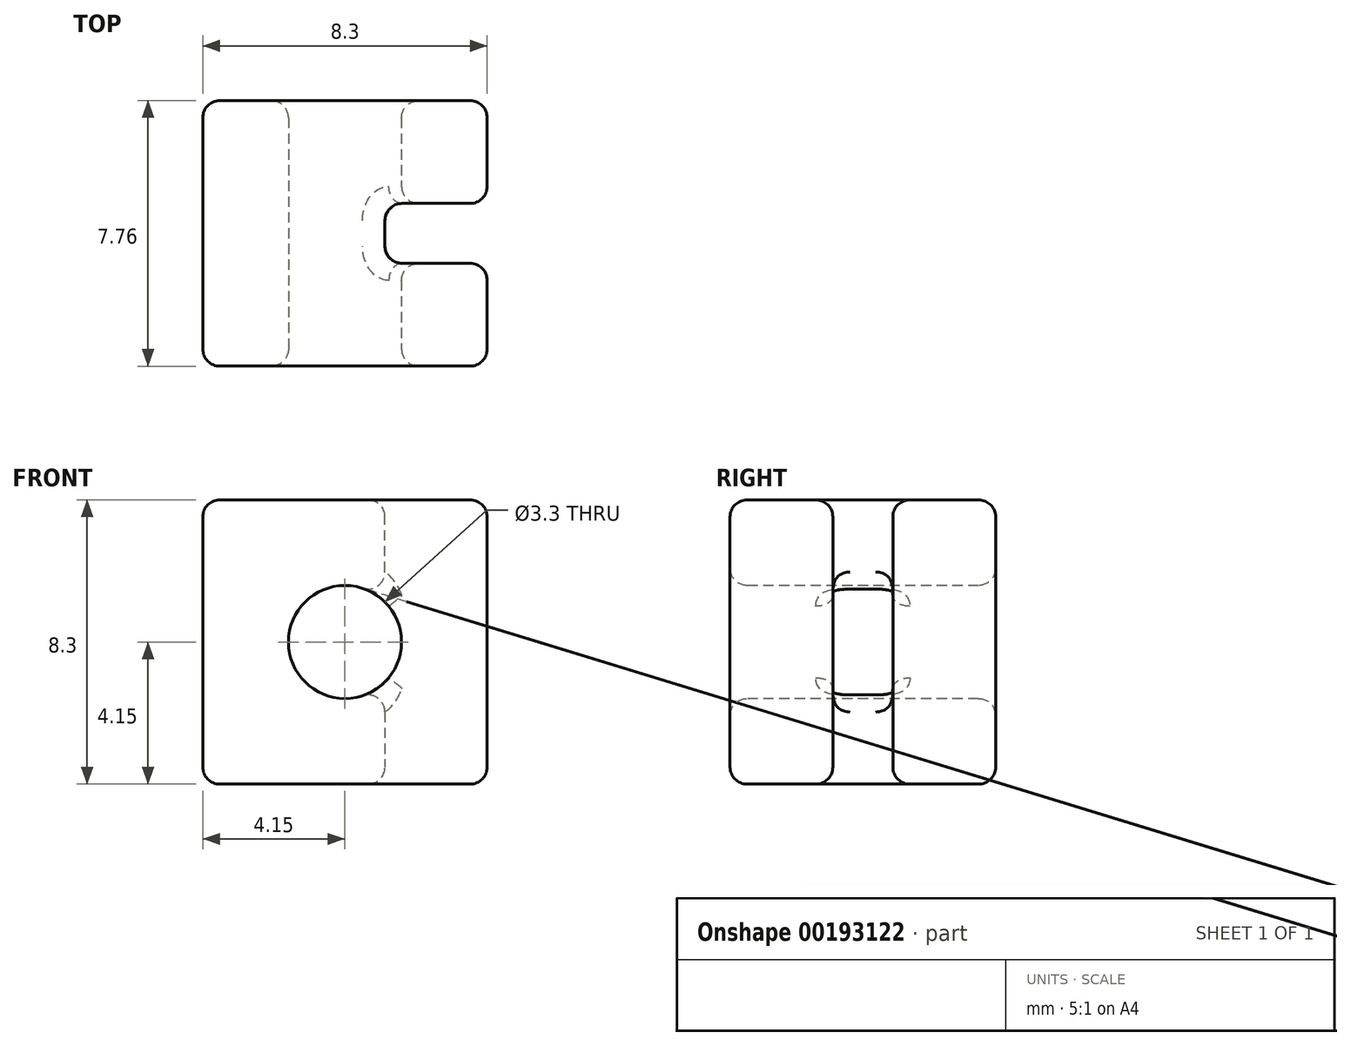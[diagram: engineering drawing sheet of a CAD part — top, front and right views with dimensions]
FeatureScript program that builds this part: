
annotation { "Feature Type Name" : "Feature", "Feature Type Description" : "" }
export const myFeature = defineFeature(function(context is Context, id is Id, definition is map)
    precondition{}
    {
        {
            var Q0;
            Q0=qCreatedBy(makeId("Front.planeOp"),FACE);
            var sketch = newSketch(context, id + "F0", { "sketchPlane" : qUnion([Q0])});
            skCircle(sketch, "E0", {"center": v(0, 0) * mm, "radius": 1.65 * mm});
            skLineSegment(sketch, "E1.bottom", {"start": v(-4.15, 4.15) * mm, "end": v(4.15, 4.15) * mm});
            skLineSegment(sketch, "E1.top", {"start": v(-4.15, -4.15) * mm, "end": v(4.15, -4.15) * mm});
            skLineSegment(sketch, "E1.left", {"start": v(-4.15, 4.15) * mm, "end": v(-4.15, -4.15) * mm});
            skLineSegment(sketch, "E1.right", {"start": v(4.15, 4.15) * mm, "end": v(4.15, -4.15) * mm});
            skLineSegment(sketch, "E2", {"start": v(-4.15, 4.15) * mm, "end": v(4.15, -4.15) * mm, "construction": true});
            skLineSegment(sketch, "E3", {"start": v(-4.15, -4.15) * mm, "end": v(4.15, 4.15) * mm, "construction": true});
            skPoint(sketch, "E4", {"position": v(1.17, 1.17) * mm});
            skPoint(sketch, "E5", {"position": v(1.17, -1.17) * mm});
            skLineSegment(sketch, "E6", {"start": v(1.17, 1.17) * mm, "end": v(1.17, 4.15) * mm});
            skLineSegment(sketch, "E7", {"start": v(1.17, -1.17) * mm, "end": v(1.17, -4.15) * mm});
            skSolve(sketch);
        }
        {
            var Q0;
            Q0=qCreatedBy(makeId("Right.planeOp"),FACE);
            var sketch = newSketch(context, id + "F1", { "sketchPlane" : qUnion([Q0])});
            skLineSegment(sketch, "E8.bottom", {"start": v(-0.87, -4.15) * mm, "end": v(0.87, -4.15) * mm});
            skLineSegment(sketch, "E8.top", {"start": v(-0.87, 4.15) * mm, "end": v(0.87, 4.15) * mm});
            skLineSegment(sketch, "E8.left", {"start": v(-0.87, -4.15) * mm, "end": v(-0.87, 4.15) * mm});
            skLineSegment(sketch, "E8.right", {"start": v(0.88, -4.15) * mm, "end": v(0.88, 4.15) * mm});
            skPoint(sketch, "E8.middle", {"position": v(0, 0) * mm});
            skLineSegment(sketch, "E9.bottom", {"start": v(3.87, 4.15) * mm, "end": v(0.87, 4.15) * mm});
            skLineSegment(sketch, "E9.top", {"start": v(3.88, -4.15) * mm, "end": v(0.87, -4.15) * mm});
            skLineSegment(sketch, "E9.left", {"start": v(3.87, 4.15) * mm, "end": v(3.88, -4.15) * mm});
            skLineSegment(sketch, "E9.right", {"start": v(0.88, 4.15) * mm, "end": v(0.88, -4.15) * mm});
            skLineSegment(sketch, "E10.bottom", {"start": v(-0.88, 4.15) * mm, "end": v(-3.87, 4.15) * mm});
            skLineSegment(sketch, "E10.top", {"start": v(-0.87, -4.15) * mm, "end": v(-3.87, -4.15) * mm});
            skLineSegment(sketch, "E10.left", {"start": v(-0.88, 4.15) * mm, "end": v(-0.87, -4.15) * mm});
            skLineSegment(sketch, "E10.right", {"start": v(-3.87, 4.15) * mm, "end": v(-3.87, -4.15) * mm});
            skSolve(sketch);
        }
        {
            var Q0;
            {var subQ0=sQuery(id+"F0.wireOp",EDGE,"E1.left");Q0=makeQuery(id+"F0.imprint","IMPRINT",FACE,{"disambiguationData":[TD([[makeQuery(id+"F0.imprint","IMPRINT",EDGE,{"derivedFrom":subQ0}),1.0]])]});}
            var Q1;
            Q1=sQuery(id+"F1.wireOp",VERTEX,"E9.bottom.end");
            var Q2;
            Q2=sQuery(id+"F1.wireOp",VERTEX,"E8.left.end");
            extrude(context, id + "F2", {"entities" : qUnion([Q0]), "endBound" : BoundingType.UP_TO_VERTEX, "oppositeDirection" : true, "endBoundEntityVertex" : qUnion([Q1]), "depth" : 25 * mm, "hasSecondDirection" : true, "secondDirectionBound" : SecondDirectionBoundingType.UP_TO_VERTEX, "secondDirectionOppositeDirection" : false, "secondDirectionBoundEntityVertex" : qUnion([Q2]), "secondDirectionDepth" : 25 * mm});
        }
        {
            var Q0;
            Q0 = qSketchRegion(id + "F0", true);
            var Q1;
            Q1=sQuery(id+"F1.wireOp",VERTEX,"E9.left.start");
            var Q2;
            Q2=makeQuery(id+"F2.opExtrude","CAP_FACE",FACE,{"disambiguationData":[OSD([sQuery(id+"F0.wireOp",EDGE,"E0"),sQuery(id+"F0.wireOp",EDGE,"E1.bottom"),sQuery(id+"F0.wireOp",EDGE,"E1.top"),sQuery(id+"F0.wireOp",EDGE,"E1.left"),sQuery(id+"F0.wireOp",EDGE,"E6"),sQuery(id+"F0.wireOp",EDGE,"E7")])],"isStart":false});
            extrude(context, id + "F3", {"entities" : qUnion([Q0]), "operationType" : NewBodyOperationType.ADD, "endBound" : BoundingType.UP_TO_VERTEX, "oppositeDirection" : true, "endBoundEntityVertex" : qUnion([Q1]), "depth" : 3.25 * mm, "hasSecondDirection" : true, "secondDirectionBound" : SecondDirectionBoundingType.UP_TO_SURFACE, "secondDirectionOppositeDirection" : true, "secondDirectionBoundEntityFace" : qUnion([Q2]), "secondDirectionDepth" : 2.3 * mm});
        }
        {
            var Q0;
            Q0 = qSketchRegion(id + "F0", true);
            var Q1;
            Q1=sQuery(id+"F1.wireOp",VERTEX,"E10.bottom.end");
            var Q2;
            Q2=makeQuery(id+"F2.opExtrude","CAP_FACE",FACE,{"disambiguationData":[OSD([sQuery(id+"F0.wireOp",EDGE,"E0"),sQuery(id+"F0.wireOp",EDGE,"E1.bottom"),sQuery(id+"F0.wireOp",EDGE,"E1.top"),sQuery(id+"F0.wireOp",EDGE,"E1.left"),sQuery(id+"F0.wireOp",EDGE,"E6"),sQuery(id+"F0.wireOp",EDGE,"E7")])],"isStart":true});
            extrude(context, id + "F4", {"entities" : qUnion([Q0]), "operationType" : NewBodyOperationType.ADD, "endBound" : BoundingType.UP_TO_VERTEX, "endBoundEntityVertex" : qUnion([Q1]), "depth" : 25 * mm, "hasSecondDirection" : true, "secondDirectionBound" : SecondDirectionBoundingType.UP_TO_SURFACE, "secondDirectionOppositeDirection" : false, "secondDirectionBoundEntityFace" : qUnion([Q2]), "secondDirectionDepth" : 14.2 * mm});
        }
        {
            var Q0;
            {var subQ0=sQuery(id+"F0.wireOp",EDGE,"E1.bottom");Q0=makeQuery(id+"F4.boolean.opBoolean","MERGE",FACE,{"derivedFrom":[makeQuery(id+"F3.boolean.opBoolean","MERGE",FACE,{"derivedFrom":[makeQuery(id+"F2.opExtrude","SWEPT_FACE",FACE,{"disambiguationData":[OSD([subQ0])]}),makeQuery(id+"F3.opExtrude","SWEPT_FACE",FACE,{"disambiguationData":[OSD([subQ0])]})]}),makeQuery(id+"F4.opExtrude","SWEPT_FACE",FACE,{"disambiguationData":[OSD([subQ0])]})]});}
            var Q1;
            Q1=makeQuery(id+"F4.opExtrude","SWEPT_FACE",FACE,{"disambiguationData":[OSD([sQuery(id+"F0.wireOp",EDGE,"E1.right")])]});
            var Q2;
            Q2=makeQuery(id+"F3.opExtrude","SWEPT_FACE",FACE,{"disambiguationData":[OSD([sQuery(id+"F0.wireOp",EDGE,"E1.right")])]});
            var Q3;
            Q3=makeQuery(id+"F4.opExtrude","CAP_FACE",FACE,{"disambiguationData":[OSD([sQuery(id+"F0.wireOp",EDGE,"E0"),sQuery(id+"F0.wireOp",EDGE,"E1.bottom"),sQuery(id+"F0.wireOp",EDGE,"E1.top"),sQuery(id+"F0.wireOp",EDGE,"E1.left"),sQuery(id+"F0.wireOp",EDGE,"E1.right")])],"isStart":false});
            var Q4;
            {var subQ0=sQuery(id+"F0.wireOp",EDGE,"E1.top");Q4=makeQuery(id+"F4.boolean.opBoolean","MERGE",FACE,{"derivedFrom":[makeQuery(id+"F3.boolean.opBoolean","MERGE",FACE,{"derivedFrom":[makeQuery(id+"F2.opExtrude","SWEPT_FACE",FACE,{"disambiguationData":[OSD([subQ0])]}),makeQuery(id+"F3.opExtrude","SWEPT_FACE",FACE,{"disambiguationData":[OSD([subQ0])]})]}),makeQuery(id+"F4.opExtrude","SWEPT_FACE",FACE,{"disambiguationData":[OSD([subQ0])]})]});}
            var Q5;
            {var subQ0=sQuery(id+"F0.wireOp",EDGE,"E1.left");Q5=makeQuery(id+"F4.boolean.opBoolean","MERGE",FACE,{"derivedFrom":[makeQuery(id+"F3.boolean.opBoolean","MERGE",FACE,{"derivedFrom":[makeQuery(id+"F2.opExtrude","SWEPT_FACE",FACE,{"disambiguationData":[OSD([subQ0])]}),makeQuery(id+"F3.opExtrude","SWEPT_FACE",FACE,{"disambiguationData":[OSD([subQ0])]})]}),makeQuery(id+"F4.opExtrude","SWEPT_FACE",FACE,{"disambiguationData":[OSD([subQ0])]})]});}
            var Q6;
            Q6=makeQuery(id+"F3.opExtrude","CAP_FACE",FACE,{"disambiguationData":[OSD([sQuery(id+"F0.wireOp",EDGE,"E0"),sQuery(id+"F0.wireOp",EDGE,"E1.bottom"),sQuery(id+"F0.wireOp",EDGE,"E1.top"),sQuery(id+"F0.wireOp",EDGE,"E1.left"),sQuery(id+"F0.wireOp",EDGE,"E1.right")])],"isStart":false});
            var Q7;
            Q7=makeQuery(id+"F2.opExtrude","SWEPT_FACE",FACE,{"disambiguationData":[OSD([sQuery(id+"F0.wireOp",EDGE,"E6")])]});
            var Q8;
            Q8=makeQuery(id+"F2.opExtrude","SWEPT_FACE",FACE,{"disambiguationData":[OSD([sQuery(id+"F0.wireOp",EDGE,"E7")])]});
            var Q9;
            Q9=makeQuery(id+"F3.opExtrude","CAP_FACE",FACE,{"disambiguationData":[OSD([sQuery(id+"F0.wireOp",EDGE,"E0"),sQuery(id+"F0.wireOp",EDGE,"E1.bottom"),sQuery(id+"F0.wireOp",EDGE,"E1.top"),sQuery(id+"F0.wireOp",EDGE,"E1.left"),sQuery(id+"F0.wireOp",EDGE,"E1.right")])],"isStart":true});
            var Q10;
            Q10=makeQuery(id+"F4.opExtrude","CAP_FACE",FACE,{"disambiguationData":[OSD([sQuery(id+"F0.wireOp",EDGE,"E0"),sQuery(id+"F0.wireOp",EDGE,"E1.bottom"),sQuery(id+"F0.wireOp",EDGE,"E1.top"),sQuery(id+"F0.wireOp",EDGE,"E1.left"),sQuery(id+"F0.wireOp",EDGE,"E1.right")])],"isStart":true});
            fillet(context, id + "F5", {"entities" : qUnion([Q0, Q1, Q2, Q3, Q4, Q5, Q6, Q7, Q8, Q9, Q10]), "radius" : 0.5 * mm, "tangentPropagation" : true, "allowEdgeOverflow" : false});
        }
    });
